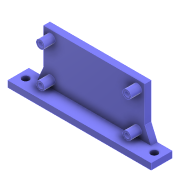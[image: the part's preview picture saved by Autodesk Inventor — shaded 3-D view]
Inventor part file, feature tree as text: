
AUTODESK INVENTOR PART (.ipt)
format: ipt  version: 2022 (Build 260153000, 153)  size: 187,392 bytes
history: native  units: mm
features: sketch x6, extrude x3, hole x2, rib x1, mirror x1, projected_geometry x1
ambient origin geometry x8: Origin, YZ Plane, XZ Plane, XY Plane, X Axis, Y Axis, Z Axis, Center Point
bodies: Solid1 (feature_tree)
feature tree (14):
  extrude  "Extrusion1"  Depth=44.0mm
  extrude  "Extrusion2"  Depth=3.0mm TaperAngle=0.0deg
  hole  "Hole1"  [1 undecoded]
  extrude  "Extrusion3"  Depth=2.0mm
  rib  "Rib2"
  hole  "Hole3"  [1 undecoded]
  mirror  "Mirror1"
  sketch  "Sketch1"  dims[d0=20.0mm d1=44.0mm]
  sketch  "Sketch2"  dims[d2=2.0mm d3=3.0mm d4=0.0mm]
  sketch  "Sketch3"  dims[d6=3.0mm d7=0.0mm d8=2.0mm]
  sketch  "Sketch6"  dims[d9=2.0mm d10=2.0mm]
  sketch  "Sketch7"  dims[d11=2.0mm]
  sketch  "Sketch8"  dims[d14=2.4mm d15=6.0mm d16=4.0mm d17=2.0mm d18=90.0deg d19=6.0mm d20=0.0mm d43=0.5mm d44=44.0mm d45=20.0mm d46=4.0mm d47=4.0mm d49=4.0mm d50=4.0mm d51=5.0mm d52=0.0mm d55=3.0mm d57=1.0mm d58=3.0mm d59=0.0mm d60=0.0mm d61=1.0mm d62=1.0mm d63=3.4mm d64=6.0mm d65=4.0mm d66=2.0mm d67=90.0deg d68=8.0mm d69=20.594885mm d70=10.0mm d71=10.0mm]
  projected_geometry  "Project Cut Edges3"
note: 2 required parameter values undecoded (feature->parameter linkage not recoverable at this tier; creation-order binding heuristic only, values carry confidence <= 0.55)
